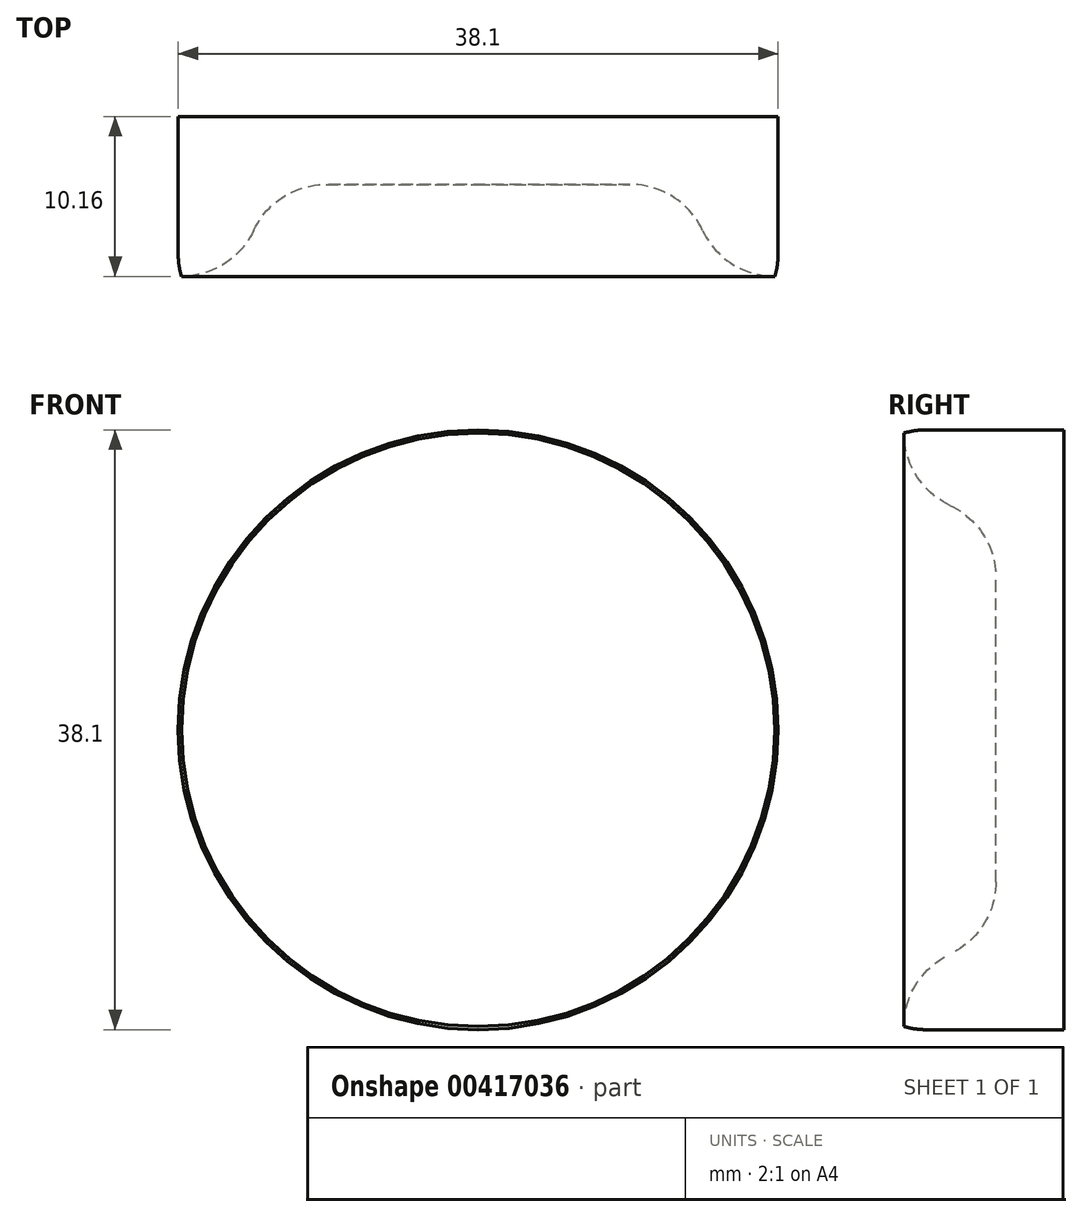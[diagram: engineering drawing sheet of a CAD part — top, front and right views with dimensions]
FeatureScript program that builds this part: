
annotation { "Feature Type Name" : "Feature", "Feature Type Description" : "" }
export const myFeature = defineFeature(function(context is Context, id is Id, definition is map)
    precondition{}
    {
        {
            var Q0;
            Q0=qCreatedBy(makeId("Front.planeOp"),FACE);
            var sketch = newSketch(context, id + "F0", { "sketchPlane" : qUnion([Q0])});
            skCircle(sketch, "E0", {"center": v(0, 0) * mm, "radius": 19.05 * mm});
            skSolve(sketch);
        }
        {
            var Q0;
            Q0=makeQuery(id+"F0.imprint","IMPRINT",FACE,{"disambiguationData":[TD([[makeQuery(id+"F0.imprint","IMPRINT",EDGE,{"derivedFrom":sQuery(id+"F0.wireOp",EDGE,"E0")}),1.0]])]});
            extrude(context, id + "F1", {"entities" : qUnion([Q0]), "depth" : 10.16 * mm});
        }
        {
            var Q0;
            Q0=makeQuery(id+"F1.opExtrude","CAP_FACE",FACE,{"disambiguationData":[OSD([sQuery(id+"F0.wireOp",EDGE,"E0")])],"isStart":false});
            shell(context, id + "F2", {"entities" : qUnion([Q0]), "thickness" : 4.32 * mm});
        }
        {
            var Q0;
            {var subQ0=sQuery(id+"F0.wireOp",EDGE,"E0");Q0=makeQuery(id+"F2.opShell","OFFSET_EDGE",EDGE,{"disambiguationData":[OSD([subQ0]),TDD([makeQuery(id+"F1.opExtrude","CAP_EDGE",EDGE,{"disambiguationData":[OSD([subQ0])],"isStart":true})])]});}
            fillet(context, id + "F3", {"entities" : qUnion([Q0]), "radius" : 5.08 * mm, "tangentPropagation" : true, "allowEdgeOverflow" : false});
        }
        {
            var Q0;
            {var subQ0=sQuery(id+"F0.wireOp",EDGE,"E0");Q0=makeQuery(id+"F2.opShell","OFFSET_EDGE",EDGE,{"disambiguationData":[OSD([subQ0]),TDD([makeQuery(id+"F1.opExtrude","CAP_EDGE",EDGE,{"disambiguationData":[OSD([subQ0])],"isStart":false})])]});}
            fillet(context, id + "F4", {"entities" : qUnion([Q0]), "radius" : 5.08 * mm, "tangentPropagation" : true, "allowEdgeOverflow" : false});
        }
        {
            var Q0;
            Q0=makeQuery(id+"F1.opExtrude","CAP_EDGE",EDGE,{"disambiguationData":[OSD([sQuery(id+"F0.wireOp",EDGE,"E0")])],"isStart":false});
            fillet(context, id + "F5", {"entities" : qUnion([Q0]), "radius" : 5.08 * mm, "tangentPropagation" : true, "allowEdgeOverflow" : false});
        }
    });
